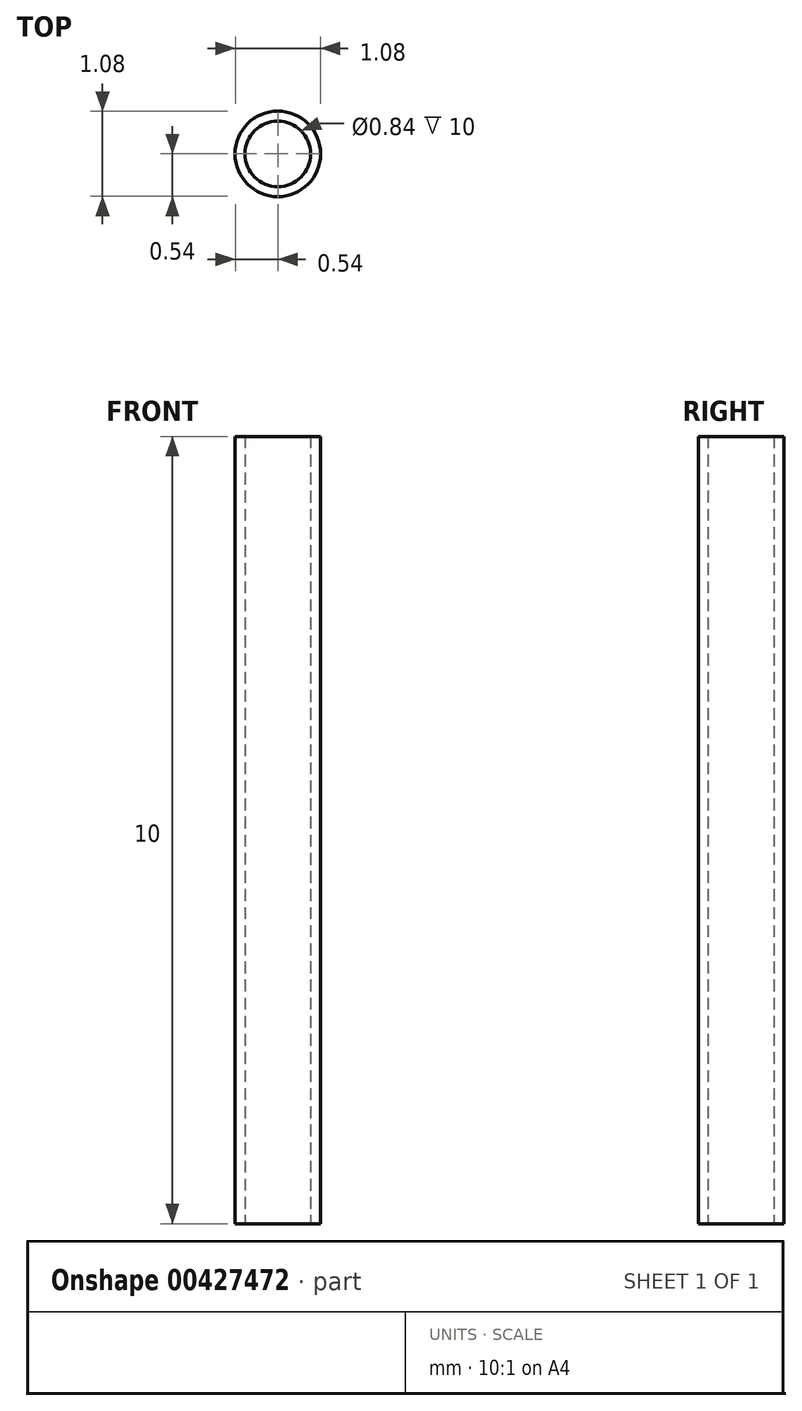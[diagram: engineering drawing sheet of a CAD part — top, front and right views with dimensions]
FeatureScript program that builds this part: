
annotation { "Feature Type Name" : "Feature", "Feature Type Description" : "" }
export const myFeature = defineFeature(function(context is Context, id is Id, definition is map)
    precondition{}
    {
        {
            var Q0;
            Q0=qCreatedBy(makeId("Top.planeOp"),FACE);
            var sketch = newSketch(context, id + "F0", { "sketchPlane" : qUnion([Q0])});
            skCircle(sketch, "E0", {"center": v(0, 0) * mm, "radius": 0.54 * mm});
            skCircle(sketch, "E1", {"center": v(0, 0) * mm, "radius": 0.42 * mm});
            skSolve(sketch);
        }
        {
            var Q0;
            Q0=makeQuery(id+"F0.imprint","IMPRINT",FACE,{"disambiguationData":[TD([[makeQuery(id+"F0.imprint","IMPRINT",EDGE,{"derivedFrom":sQuery(id+"F0.wireOp",EDGE,"E0")}),1.0]])]});
            extrude(context, id + "F1", {"entities" : qUnion([Q0]), "depth" : 10 * mm});
        }
    });
